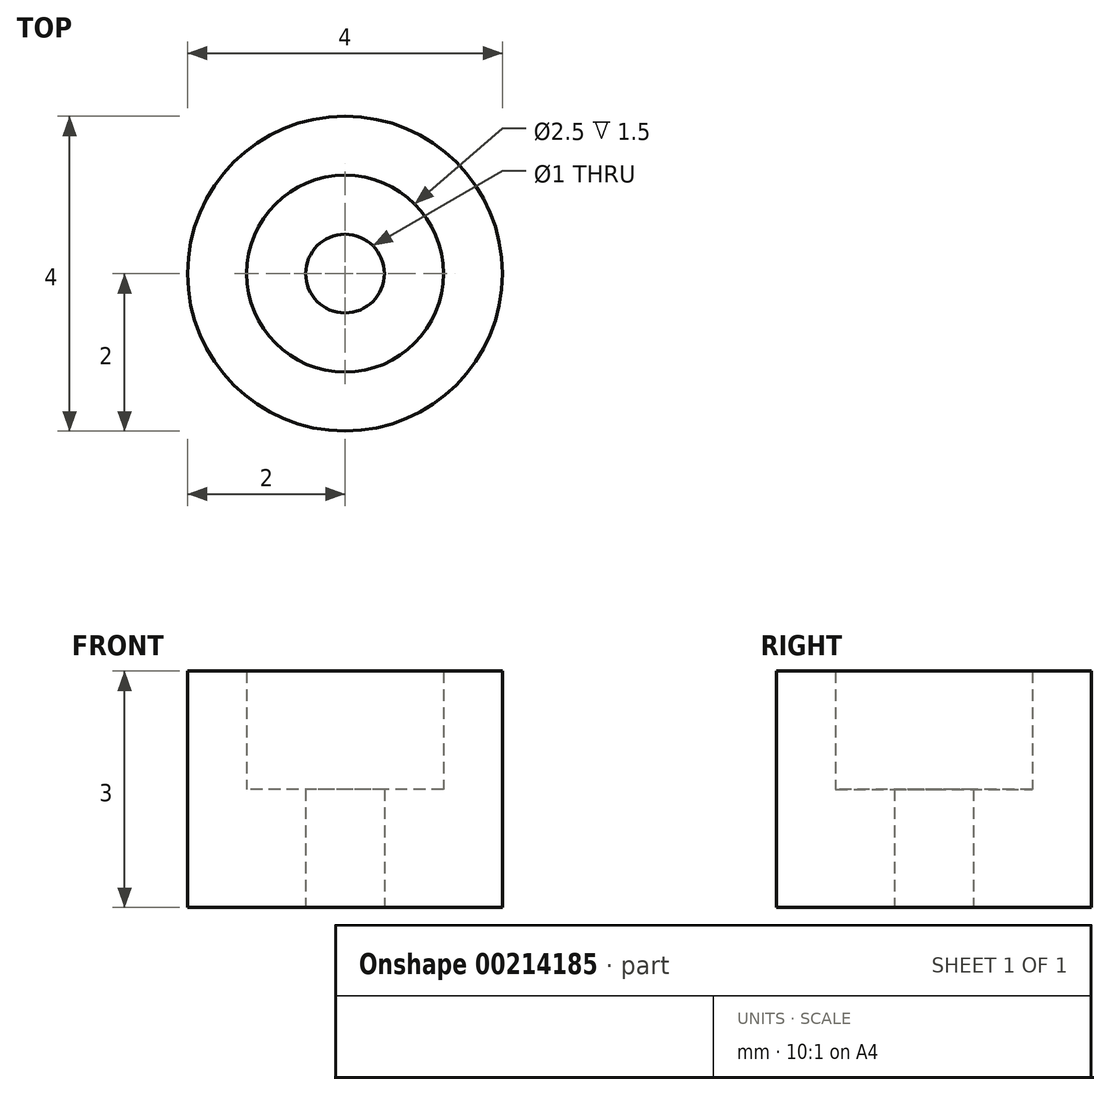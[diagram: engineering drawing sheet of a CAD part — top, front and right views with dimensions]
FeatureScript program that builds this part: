
annotation { "Feature Type Name" : "Feature", "Feature Type Description" : "" }
export const myFeature = defineFeature(function(context is Context, id is Id, definition is map)
    precondition{}
    {
        {
            var Q0;
            Q0=qCreatedBy(makeId("Top.planeOp"),FACE);
            var sketch = newSketch(context, id + "F0", { "sketchPlane" : qUnion([Q0])});
            skCircle(sketch, "E0", {"center": v(0, 0) * mm, "radius": 2 * mm});
            skCircle(sketch, "E1", {"center": v(0, 0) * mm, "radius": 1.25 * mm});
            skCircle(sketch, "E2", {"center": v(0, 0) * mm, "radius": 0.5 * mm});
            skSolve(sketch);
        }
        {
            var Q0;
            Q0 = qSketchRegion(id + "F0", true);
            extrude(context, id + "F1", {"entities" : qUnion([Q0]), "depth" : 3 * mm, "offsetDistance" : 25 * mm});
        }
        {
            var Q0;
            Q0=makeQuery(id+"F0.imprint","IMPRINT",FACE,{"disambiguationData":[TD([[makeQuery(id+"F0.imprint","IMPRINT",EDGE,{"derivedFrom":sQuery(id+"F0.wireOp",EDGE,"E1")}),1.0]])]});
            var Q1;
            Q1=makeQuery(id+"F0.imprint","IMPRINT",FACE,{"disambiguationData":[TD([[makeQuery(id+"F0.imprint","IMPRINT",EDGE,{"derivedFrom":sQuery(id+"F0.wireOp",EDGE,"E2")}),1.0]])]});
            extrude(context, id + "F2", {"entities" : qUnion([Q0, Q1]), "operationType" : NewBodyOperationType.ADD, "depth" : 1.5 * mm, "offsetDistance" : 25 * mm});
        }
        {
            var Q0;
            Q0=makeQuery(id+"F0.imprint","IMPRINT",FACE,{"disambiguationData":[TD([[makeQuery(id+"F0.imprint","IMPRINT",EDGE,{"derivedFrom":sQuery(id+"F0.wireOp",EDGE,"E2")}),1.0]])]});
            extrude(context, id + "F3", {"entities" : qUnion([Q0]), "operationType" : NewBodyOperationType.REMOVE, "depth" : 25 * mm, "offsetDistance" : 25 * mm});
        }
    });
